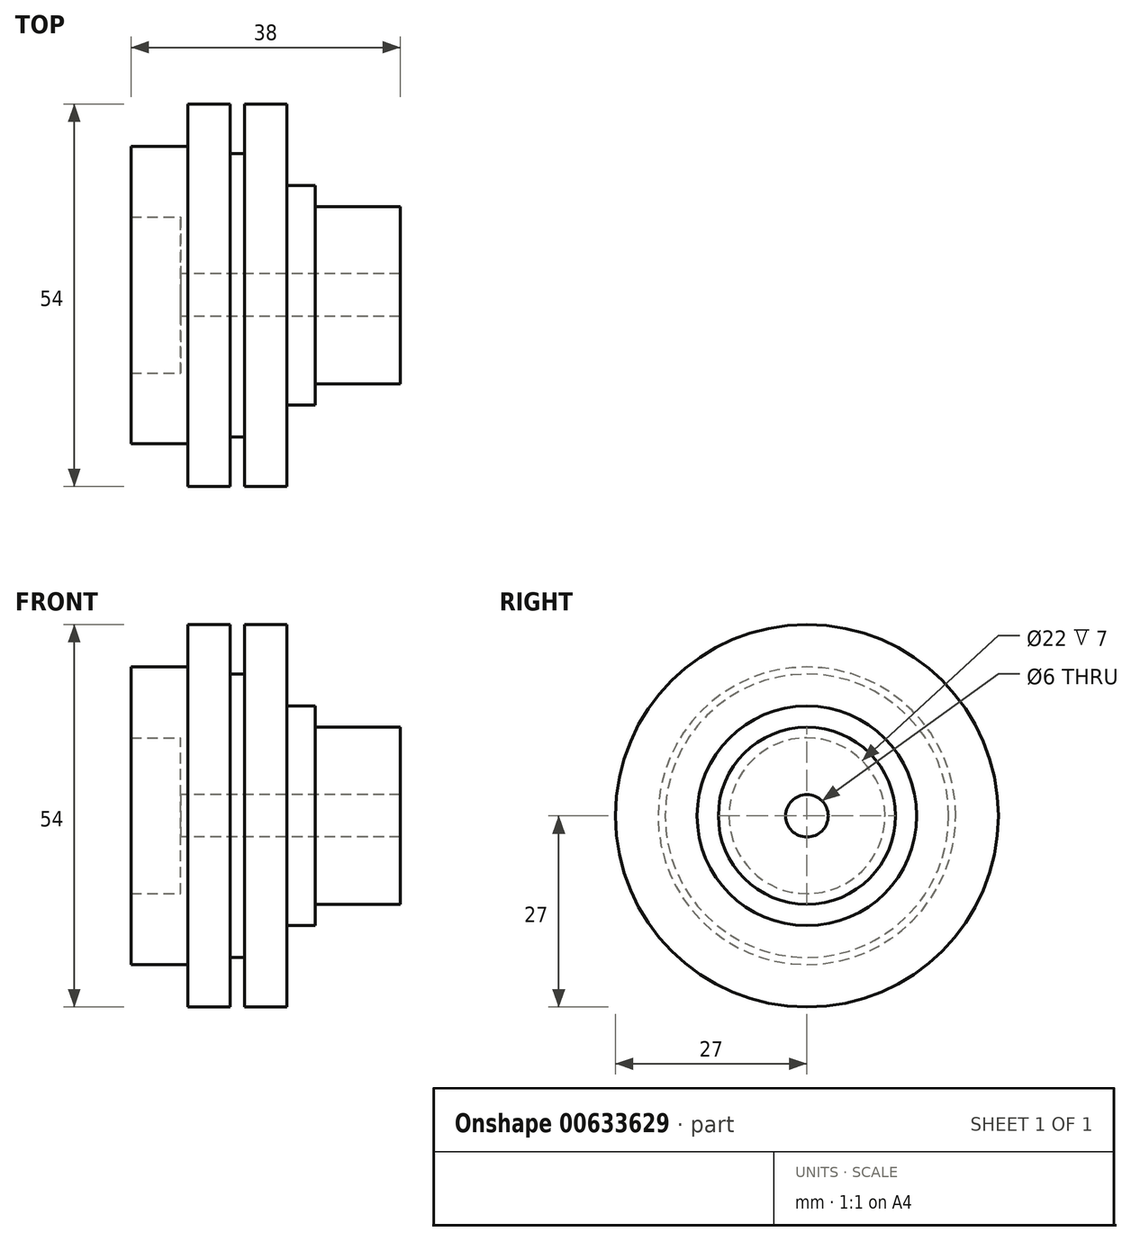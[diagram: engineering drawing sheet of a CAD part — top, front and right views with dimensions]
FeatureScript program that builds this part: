
annotation { "Feature Type Name" : "Feature", "Feature Type Description" : "" }
export const myFeature = defineFeature(function(context is Context, id is Id, definition is map)
    precondition{}
    {
        {
            var Q0;
            Q0=qCreatedBy(makeId("Front.planeOp"),FACE);
            var sketch = newSketch(context, id + "F0", { "sketchPlane" : qUnion([Q0])});
            skLineSegment(sketch, "E0", {"start": v(-31, 0) * mm, "end": v(-31, 11) * mm});
            skLineSegment(sketch, "E1", {"start": v(-31, 11) * mm, "end": v(-38, 11) * mm});
            skLineSegment(sketch, "E2", {"start": v(-24, 27) * mm, "end": v(-24, 20) * mm});
            skLineSegment(sketch, "E3", {"start": v(-24, 20) * mm, "end": v(-22, 20) * mm});
            skLineSegment(sketch, "E4", {"start": v(-22, 20) * mm, "end": v(-22, 27) * mm});
            skLineSegment(sketch, "E5", {"start": v(-22, 27) * mm, "end": v(-16, 27) * mm});
            skLineSegment(sketch, "E6", {"start": v(-16, 27) * mm, "end": v(-16, 15.5) * mm});
            skLineSegment(sketch, "E7", {"start": v(-16, 15.5) * mm, "end": v(-12, 15.5) * mm});
            skLineSegment(sketch, "E8", {"start": v(-12, 15.5) * mm, "end": v(-12, 12.5) * mm});
            skLineSegment(sketch, "E9", {"start": v(-12, 12.5) * mm, "end": v(0, 12.5) * mm});
            skLineSegment(sketch, "E10", {"start": v(0, 12.5) * mm, "end": v(0, 0) * mm});
            skLineSegment(sketch, "E11", {"start": v(0, 0) * mm, "end": v(-31, 0) * mm});
            skLineSegment(sketch, "E12", {"start": v(-38, 11) * mm, "end": v(-38, 21) * mm});
            skLineSegment(sketch, "E13", {"start": v(-38, 21) * mm, "end": v(-30, 21) * mm});
            skLineSegment(sketch, "E14", {"start": v(-30, 21) * mm, "end": v(-30, 27) * mm});
            skLineSegment(sketch, "E15", {"start": v(-30, 27) * mm, "end": v(-24, 27) * mm});
            skSolve(sketch);
        }
        {
            var Q0;
            Q0=makeQuery(id+"F0.imprint","IMPRINT",FACE,{"disambiguationData":[TD([[makeQuery(id+"F0.imprint","IMPRINT",EDGE,{"derivedFrom":sQuery(id+"F0.wireOp",EDGE,"E0")}),-1.0]])]});
            var Q1;
            Q1=sQuery(id+"F0.wireOp",EDGE,"E11");
            revolve(context, id + "F1", {"entities" : qUnion([Q0]), "axis" : qUnion([Q1]), "revolveType" : RevolveType.FULL});
        }
        {
            var Q0;
            Q0=makeQuery(id+"F1.opRevolve","SWEPT_FACE",FACE,{"disambiguationData":[OSD([sQuery(id+"F0.wireOp",EDGE,"E0")])]});
            var sketch = newSketch(context, id + "F2", { "sketchPlane" : qUnion([Q0])});
            skCircle(sketch, "E16", {"center": v(0, 0) * mm, "radius": 3 * mm});
            skSolve(sketch);
        }
        {
            var Q0;
            Q0=makeQuery(id+"F2.imprint","IMPRINT",FACE,{"disambiguationData":[TD([[makeQuery(id+"F2.imprint","IMPRINT",EDGE,{"derivedFrom":sQuery(id+"F2.wireOp",EDGE,"E16")}),1.0]])]});
            extrude(context, id + "F3", {"entities" : qUnion([Q0]), "operationType" : NewBodyOperationType.REMOVE, "endBound" : BoundingType.THROUGH_ALL, "oppositeDirection" : true, "depth" : 25 * mm, "offsetDistance" : 25 * mm});
        }
    });
